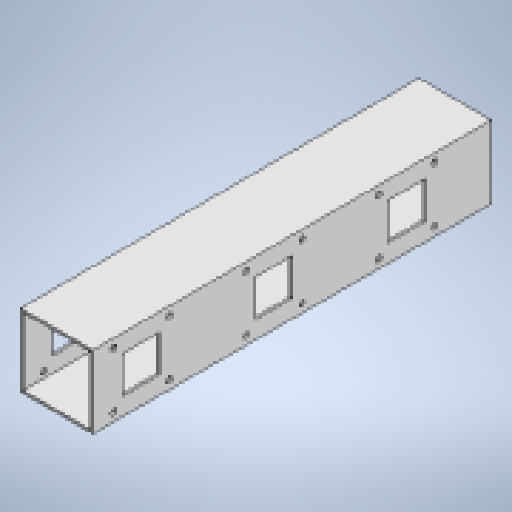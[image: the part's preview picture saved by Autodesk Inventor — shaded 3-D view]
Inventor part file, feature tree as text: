
AUTODESK INVENTOR PART (.ipt)
format: ipt  version: 2025.3 (Build 293356030, 356C)  size: 234,496 bytes
history: native  units: mm
features: extrude x2, sketch x2, pattern_linear x1
ambient origin geometry x8: Origin, YZ Plane, XZ Plane, XY Plane, X Axis, Y Axis, Z Axis, Center Point
bodies: Body1 (feature_tree)
feature tree (5):
  extrude  "Extrusion3"  Depth=60.0mm
  extrude  "Extrusion4"  Depth=2.0mm
  pattern_linear  "Rectangular Pattern4"  Count1=33 Spacing1=0.0mm
  sketch  "Sketch9"  dims[d61=500.0mm d172=60.0mm]
  sketch  "Sketch10"  dims[d173=60.0mm d174=2.0mm d175=330.0mm d176=0.0mm d179=0.0mm d180=0.0mm d181=40.0mm d187=30.5mm d188=30.5mm d189=5.0mm d190=51.0mm d191=21.92031mm d192=110.0mm d193=30.0mm d195=110.0mm d196=46.0mm]
